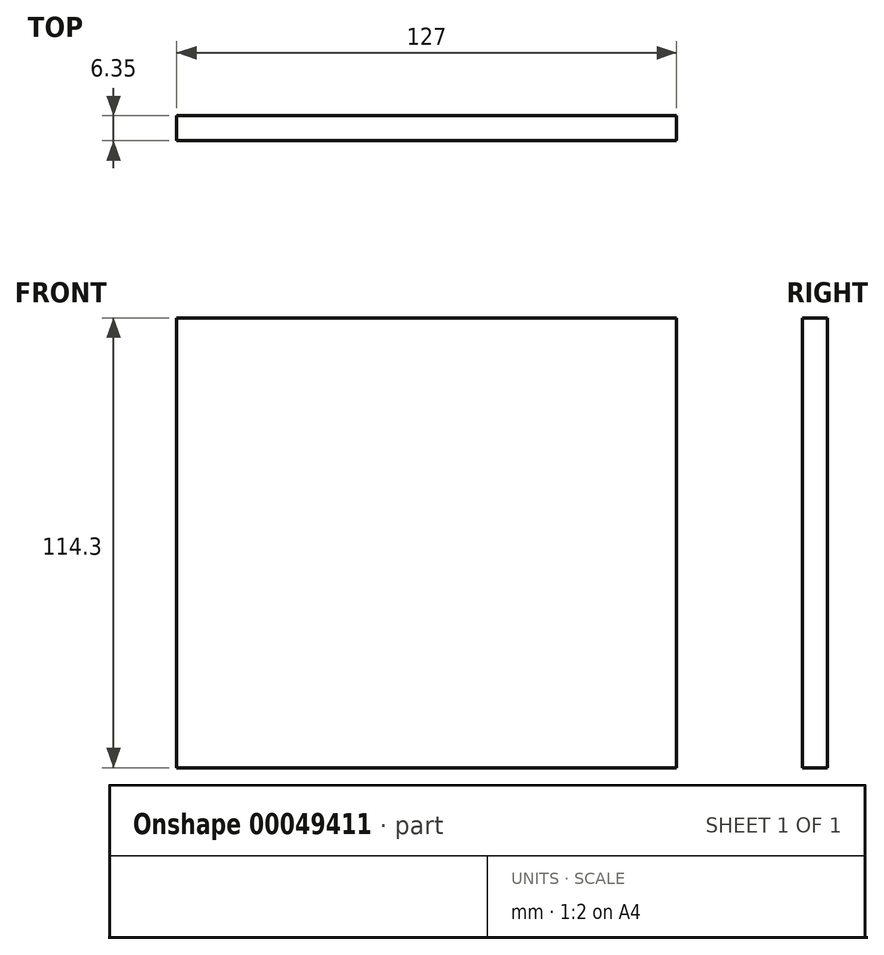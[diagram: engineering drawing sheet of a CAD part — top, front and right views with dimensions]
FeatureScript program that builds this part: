
annotation { "Feature Type Name" : "Feature", "Feature Type Description" : "" }
export const myFeature = defineFeature(function(context is Context, id is Id, definition is map)
    precondition{}
    {
        {
            var Q0;
            Q0=qCreatedBy(makeId("Front.planeOp"),FACE);
            var sketch = newSketch(context, id + "F0", { "sketchPlane" : qUnion([Q0])});
            skLineSegment(sketch, "E0.bottom", {"start": v(-246.67, 114.3) * mm, "end": v(-119.67, 114.3) * mm});
            skLineSegment(sketch, "E0.top", {"start": v(-246.67, 0) * mm, "end": v(-119.67, 0) * mm});
            skLineSegment(sketch, "E0.left", {"start": v(-246.67, 114.3) * mm, "end": v(-246.67, 0) * mm});
            skLineSegment(sketch, "E0.right", {"start": v(-119.67, 114.3) * mm, "end": v(-119.67, 0) * mm});
            skSolve(sketch);
        }
        {
            var Q0;
            Q0=makeQuery(id+"F0.imprint","IMPRINT",FACE,{"disambiguationData":[TD([[makeQuery(id+"F0.imprint","IMPRINT",EDGE,{"derivedFrom":sQuery(id+"F0.wireOp",EDGE,"E0.bottom")}),-1.0]])]});
            extrude(context, id + "F1", {"entities" : qUnion([Q0]), "depth" : 6.35 * mm});
        }
    });
